# Revit family: 2071463
name_source: partatom
category: Lighting Fixtures
units: mm (PartAtom-declared; Revit-internal decimal feet)

## family parameters
Cut with Voids When Loaded = No
Host = Face
Light Source = Yes
Maintain Annotation Orientation = No
OmniClass Number = 23.80.70.00
OmniClass Title = Lighting
Part Type = Normal
Room Calculation Point = No
Round Connector Dimension = Use Diameter
Shared = No

## types (1)
- MC2 D/I KIT 1.2M 4K DALI WHT PRIS
    Apparent Load = 31 VA
    Assembly Code = D5020200
    AssetType = Fixed
    ClassificationName = Uniclass2015
    ClassificationValue = EF_70_80
    Color Filter = 16777215
    Cost = 0 $
    Default Elevation = 1219 mm
    Description = MC2-KIT D/I 1.2M 4K DALI WHT PRIS LED luminaire, white RAL9016 finishing, direct/indirect distribution (65/35), suspended kit version is pre-wired and supplied complete with end caps and suspension cables, compact and minimalist design based on the Golden Mean, ideal for offices, meeting rooms, corridors, education facilities, museums and libraries, extruded aluminium body, diffuser: micro prismatic, colour temperature: 4000K neutral white, total system power: 29W, total fixture output: 3850lm, luminaire efficacy: 133lm/W, LOR: 100%, colour rendering: Ra >80, LED Chromacity: 3 step MacAdam ellipse, lifespan: 66,000 hours L90B10, IR/UV free light source without heat radiation, operating voltage: 220-240V / 50-60Hz, drive current: (Direct) 800mA + (Indirect) 350mA, electronic driver, DALI dimmable, direct/indirect independently addressable, electrical protection: CLASS I, IP20, suitable for internal environment only.
    Dimming Lamp Color Temperature Shift = <None>
    DimmingControlOptions = DALI
    DocumentationLiterature = https://www.sylvania-lighting.com
    ElectricShockClassification = Class I
    EmergencyLight = No
    Emit Shape Visible in Rendering = No
    Emit from Rectangle Length = 1200 mm
    Emit from Rectangle Width = 54 mm  [stored 0.177165 ft]
    IfcExportAs = IfcLightFixtureType
    IfcExportType = IfcLightFixtureType
    ImpactProtectionIndex = IK03
    IngressProtection = IP20
    InputNominalFrequency = 50/60Hz
    InputVoltage = 220-240 V
    Keynote = 16500
    Lamp = LED
    LampColourRenderingIndex = 80
    LampColourTemperature = 4000 K
    LampMacAdamStep = 3
    LampNominalLuminous = 3850 lm
    LampsType = LED
    LightOutputRatio = 100
    LuminaireType = Suspended
    LuminousEfficacy = 133 lm/W
    Manufacturer = Feilo Sylvania
    ManufacturerName = Feilo Sylvania
    Material = Aluminium
    Material_1_SYL = Metal_Sylvania_Mini Continuum II_White
    Material_2_SYL = Polycarbonate_Sylvania_Mini Continuum II_Prismatic_4000K
    Material_3_SYL = Metal_Sylvania_Mini Contiuum II_Silver
    Material_4_SYL = <By Category>
    Model = MC2 D/I KIT 1.2M 4K DALI WHT PRIS
    ModelNumber = 2071463
    ModelReference = MC2 D/I KIT 1.2M 4K DALI WHT PRIS
    Name = MC2 D/I KIT 1.2M 4K DALI WHT PRIS
    NominalDepth = 54 mm  [stored 0.177165 ft]
    NominalHeight = 86 mm  [stored 0.282152 ft]
    NominalLength = 1200 mm
    PendantMax = 3000 mm  [stored 9.84252 ft]
    PendantMin = 50 mm  [stored 0.164042 ft]
    Photometric Web File = 2071463.ies
    PowerConsumption = 29 W
    PowerFactor = 0.95
    SuspensionDistance1 = 62 mm  [stored 0.203412 ft]
    SuspensionDistance2 = 82 mm  [stored 0.269029 ft]
    Tilt Angle = -90.00°
    Type Image = <None>
    TypeName = Mini Continuum II - Direct/Indirect - Suspended Kit
    URL = http://www.sylvania-group.com
    Voltage = 230 V
    WarrantyDescription = http://www.sylvania-group.com
    WarrantyDurationParts = 5
    WarrantyDurationUnit = Years
    Weight = 3.4 kg

note: [stored X ft] marks values corroborated as IEEE doubles in the binary element streams (Revit-internal decimal feet)

## geometry (parser evidence)
native form markers: Sweep x2
no freeform markers — native parametric forms only
